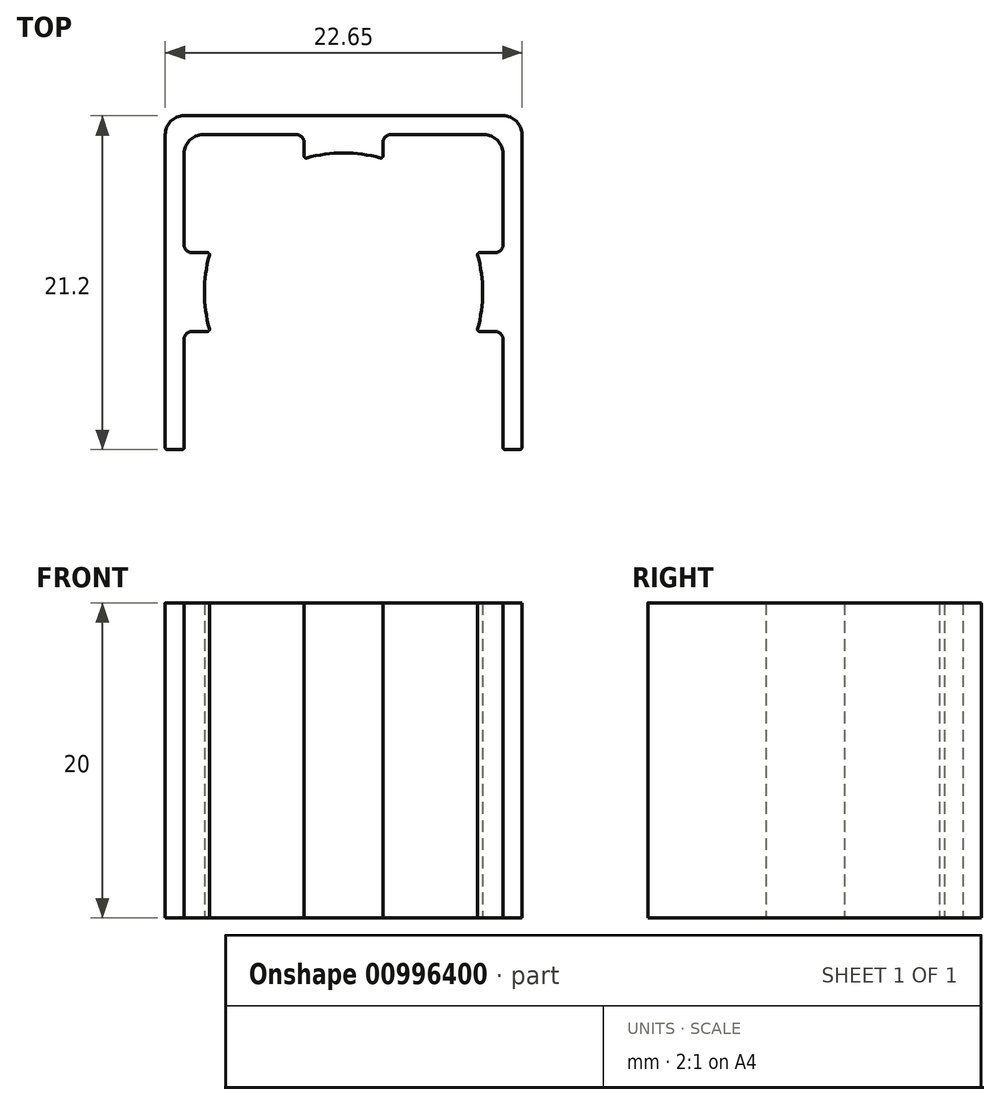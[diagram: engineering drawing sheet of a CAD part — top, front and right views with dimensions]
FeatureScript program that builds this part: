
annotation { "Feature Type Name" : "Feature", "Feature Type Description" : "" }
export const myFeature = defineFeature(function(context is Context, id is Id, definition is map)
    precondition{}
    {
        {
            var Q0;
            Q0=qCreatedBy(makeId("Top.planeOp"),FACE);
            var sketch = newSketch(context, id + "F0", { "sketchPlane" : qUnion([Q0])});
            skLineSegment(sketch, "E0", {"start": v(-3.94, -8.29) * mm, "end": v(-3.94, 11.59) * mm});
            skLineSegment(sketch, "E1", {"start": v(-2.74, 12.79) * mm, "end": v(17.5, 12.79) * mm});
            skLineSegment(sketch, "E2", {"start": v(18.7, 11.59) * mm, "end": v(18.7, -8.29) * mm});
            skLineSegment(sketch, "E3", {"start": v(18.58, -8.41) * mm, "end": v(17.63, -8.41) * mm});
            skLineSegment(sketch, "E4", {"start": v(17.5, -8.29) * mm, "end": v(17.5, -1.41) * mm});
            skLineSegment(sketch, "E5", {"start": v(16.3, 11.59) * mm, "end": v(10.38, 11.59) * mm});
            skLineSegment(sketch, "E6", {"start": v(-2.74, 10.39) * mm, "end": v(-2.74, 4.59) * mm});
            skLineSegment(sketch, "E7", {"start": v(-2.87, -8.41) * mm, "end": v(-3.82, -8.41) * mm});
            skPoint(sketch, "E8", {"position": v(4.88, 11.59) * mm});
            skPoint(sketch, "E9", {"position": v(9.88, 11.59) * mm});
            skPoint(sketch, "E10", {"position": v(-2.74, 4.09) * mm});
            skPoint(sketch, "E11", {"position": v(-2.74, -0.91) * mm});
            skPoint(sketch, "E12", {"position": v(17.5, 4.09) * mm});
            skPoint(sketch, "E13", {"position": v(17.5, -0.91) * mm});
            skLineSegment(sketch, "E14.bottom", {"start": v(-2.24, 4.09) * mm, "end": v(-1.26, 4.09) * mm});
            skLineSegment(sketch, "E14.top", {"start": v(-2.24, -0.91) * mm, "end": v(-1.26, -0.91) * mm});
            skLineSegment(sketch, "E15.bottom", {"start": v(17, 4.09) * mm, "end": v(16.02, 4.09) * mm});
            skLineSegment(sketch, "E15.top", {"start": v(17, -0.91) * mm, "end": v(16.02, -0.91) * mm});
            skLineSegment(sketch, "E16.left", {"start": v(4.88, 11.09) * mm, "end": v(4.88, 10.23) * mm});
            skLineSegment(sketch, "E16.right", {"start": v(9.88, 11.09) * mm, "end": v(9.88, 10.23) * mm});
            skLineSegment(sketch, "E17", {"start": v(-0.74, 1.59) * mm, "end": v(15.5, 1.59) * mm, "construction": true});
            skPoint(sketch, "E18", {"position": v(-1.1, -0.91) * mm});
            skPoint(sketch, "E19", {"position": v(7.38, 1.59) * mm});
            skArc(sketch, "E20", {"start": v(-1.14, 3.93) * mm, "mid": v(-1.45, 1.59) * mm, "end": v(-1.14, -0.76) * mm});
            skPoint(sketch, "E21.orphan", {"position": v(-0.74, 4.09) * mm});
            skPoint(sketch, "E14.right.end.orphan", {"position": v(-0.74, -0.91) * mm});
            skArc(sketch, "E22.trimOffspring", {"start": v(15.9, -0.76) * mm, "mid": v(16.22, 1.59) * mm, "end": v(15.9, 3.93) * mm});
            skPoint(sketch, "E23.orphan", {"position": v(9.88, 9.59) * mm});
            skArc(sketch, "E24.trimOffspring", {"start": v(9.72, 10.1) * mm, "mid": v(7.38, 10.42) * mm, "end": v(5.04, 10.1) * mm});
            skPoint(sketch, "E25.orphan", {"position": v(15.5, 4.09) * mm});
            skPoint(sketch, "E26.orphan", {"position": v(15.5, -0.91) * mm});
            skLineSegment(sketch, "E27.trimOffspring", {"start": v(17.5, 4.59) * mm, "end": v(17.5, 10.39) * mm});
            skLineSegment(sketch, "E28.trimOffspring", {"start": v(4.38, 11.59) * mm, "end": v(-1.54, 11.59) * mm});
            skLineSegment(sketch, "E29.trimOffspring", {"start": v(-2.74, -1.41) * mm, "end": v(-2.74, -8.29) * mm});
            skPoint(sketch, "E30.visualSharp", {"position": v(-2.74, 11.59) * mm});
            skArc(sketch, "E30.filletArc", {"start": v(-1.54, 11.59) * mm, "mid": v(-2.4, 11.23) * mm, "end": v(-2.74, 10.39) * mm});
            skPoint(sketch, "E31.visualSharp", {"position": v(17.5, 11.59) * mm});
            skArc(sketch, "E31.filletArc", {"start": v(17.5, 10.39) * mm, "mid": v(17.15, 11.23) * mm, "end": v(16.3, 11.59) * mm});
            skPoint(sketch, "E32.visualSharp", {"position": v(-3.94, 12.79) * mm});
            skArc(sketch, "E32.filletArc", {"start": v(-2.74, 12.79) * mm, "mid": v(-3.6, 12.43) * mm, "end": v(-3.94, 11.59) * mm});
            skPoint(sketch, "E33.visualSharp", {"position": v(18.7, 12.79) * mm});
            skArc(sketch, "E33.filletArc", {"start": v(18.7, 11.59) * mm, "mid": v(18.35, 12.43) * mm, "end": v(17.5, 12.79) * mm});
            skArc(sketch, "E34.filletArc", {"start": v(-2.74, 4.59) * mm, "mid": v(-2.6, 4.23) * mm, "end": v(-2.24, 4.09) * mm});
            skArc(sketch, "E35.filletArc", {"start": v(-2.24, -0.91) * mm, "mid": v(-2.6, -1.06) * mm, "end": v(-2.74, -1.41) * mm});
            skArc(sketch, "E36.filletArc", {"start": v(4.88, 11.09) * mm, "mid": v(4.73, 11.44) * mm, "end": v(4.38, 11.59) * mm});
            skArc(sketch, "E37.filletArc", {"start": v(10.38, 11.59) * mm, "mid": v(10.03, 11.44) * mm, "end": v(9.88, 11.09) * mm});
            skArc(sketch, "E38.filletArc", {"start": v(17, 4.09) * mm, "mid": v(17.36, 4.23) * mm, "end": v(17.5, 4.59) * mm});
            skArc(sketch, "E39.filletArc", {"start": v(17.5, -1.41) * mm, "mid": v(17.36, -1.06) * mm, "end": v(17, -0.91) * mm});
            skPoint(sketch, "E40.visualSharp", {"position": v(15.86, 4.09) * mm});
            skArc(sketch, "E40.filletArc", {"start": v(16.02, 4.09) * mm, "mid": v(15.92, 4.04) * mm, "end": v(15.9, 3.93) * mm});
            skPoint(sketch, "E41.visualSharp", {"position": v(15.86, -0.91) * mm});
            skArc(sketch, "E41.filletArc", {"start": v(15.9, -0.76) * mm, "mid": v(15.92, -0.86) * mm, "end": v(16.02, -0.91) * mm});
            skArc(sketch, "E42.filletArc", {"start": v(-1.26, -0.91) * mm, "mid": v(-1.16, -0.86) * mm, "end": v(-1.14, -0.76) * mm});
            skPoint(sketch, "E43.visualSharp", {"position": v(-1.1, 4.09) * mm});
            skArc(sketch, "E43.filletArc", {"start": v(-1.14, 3.93) * mm, "mid": v(-1.16, 4.04) * mm, "end": v(-1.26, 4.09) * mm});
            skPoint(sketch, "E44.visualSharp", {"position": v(4.88, 10.06) * mm});
            skArc(sketch, "E44.filletArc", {"start": v(4.88, 10.23) * mm, "mid": v(4.93, 10.13) * mm, "end": v(5.04, 10.1) * mm});
            skPoint(sketch, "E45.visualSharp", {"position": v(9.88, 10.06) * mm});
            skArc(sketch, "E45.filletArc", {"start": v(9.72, 10.1) * mm, "mid": v(9.83, 10.13) * mm, "end": v(9.88, 10.23) * mm});
            skPoint(sketch, "E46.visualSharp", {"position": v(-3.94, -8.41) * mm});
            skArc(sketch, "E46.filletArc", {"start": v(-3.94, -8.29) * mm, "mid": v(-3.9, -8.38) * mm, "end": v(-3.82, -8.41) * mm});
            skPoint(sketch, "E47.visualSharp", {"position": v(-2.74, -8.41) * mm});
            skArc(sketch, "E47.filletArc", {"start": v(-2.87, -8.41) * mm, "mid": v(-2.78, -8.38) * mm, "end": v(-2.74, -8.29) * mm});
            skPoint(sketch, "E48.visualSharp", {"position": v(17.5, -8.41) * mm});
            skArc(sketch, "E48.filletArc", {"start": v(17.5, -8.29) * mm, "mid": v(17.54, -8.38) * mm, "end": v(17.63, -8.41) * mm});
            skPoint(sketch, "E49.visualSharp", {"position": v(18.7, -8.41) * mm});
            skArc(sketch, "E49.filletArc", {"start": v(18.58, -8.41) * mm, "mid": v(18.67, -8.38) * mm, "end": v(18.7, -8.29) * mm});
            skSolve(sketch);
        }
        {
            var Q0;
            Q0=makeQuery(id+"F0.imprint","IMPRINT",FACE,{"disambiguationData":[TD([[makeQuery(id+"F0.imprint","IMPRINT",EDGE,{"derivedFrom":sQuery(id+"F0.wireOp",EDGE,"E0")}),-1.0]])]});
            extrude(context, id + "F1", {"entities" : qUnion([Q0]), "depth" : 20 * mm, "offsetDistance" : 25 * mm});
        }
    });
